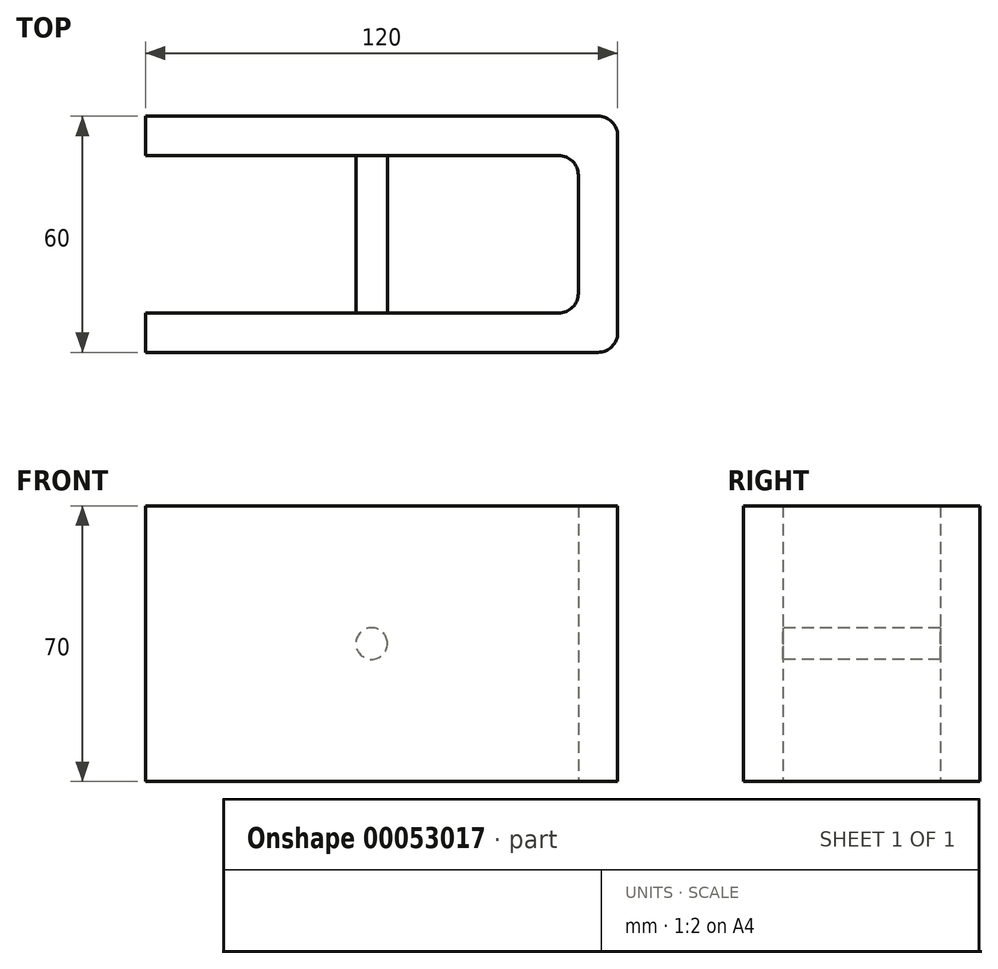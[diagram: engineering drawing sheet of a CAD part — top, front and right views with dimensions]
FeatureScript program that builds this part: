
annotation { "Feature Type Name" : "Feature", "Feature Type Description" : "" }
export const myFeature = defineFeature(function(context is Context, id is Id, definition is map)
    precondition{}
    {
        {
            var Q0;
            Q0=qCreatedBy(makeId("Top.planeOp"),FACE);
            var sketch = newSketch(context, id + "F0", { "sketchPlane" : qUnion([Q0])});
            skLineSegment(sketch, "E0", {"start": v(-61.74, 34.03) * mm, "end": v(53.26, 34.03) * mm});
            skLineSegment(sketch, "E1", {"start": v(43.26, 24.03) * mm, "end": v(-61.74, 24.03) * mm});
            skLineSegment(sketch, "E2", {"start": v(-61.74, 24.03) * mm, "end": v(-61.74, 34.03) * mm});
            skLineSegment(sketch, "E3", {"start": v(-61.74, -15.97) * mm, "end": v(-61.74, -25.97) * mm});
            skLineSegment(sketch, "E4", {"start": v(-61.74, -25.97) * mm, "end": v(53.26, -25.97) * mm});
            skLineSegment(sketch, "E5", {"start": v(43.26, -15.97) * mm, "end": v(-61.74, -15.97) * mm});
            skLineSegment(sketch, "E6", {"start": v(48.26, 19.03) * mm, "end": v(48.26, -10.97) * mm});
            skLineSegment(sketch, "E7", {"start": v(58.26, 29.03) * mm, "end": v(58.26, -20.97) * mm});
            skPoint(sketch, "E8.visualSharp", {"position": v(58.26, 34.03) * mm});
            skArc(sketch, "E8.filletArc", {"start": v(58.26, 29.03) * mm, "mid": v(56.8, 32.56) * mm, "end": v(53.26, 34.03) * mm});
            skPoint(sketch, "E9.visualSharp", {"position": v(48.26, 24.03) * mm});
            skArc(sketch, "E9.filletArc", {"start": v(48.26, 19.03) * mm, "mid": v(46.8, 22.56) * mm, "end": v(43.26, 24.03) * mm});
            skPoint(sketch, "E10.visualSharp", {"position": v(48.26, -15.97) * mm});
            skArc(sketch, "E10.filletArc", {"start": v(43.26, -15.97) * mm, "mid": v(46.8, -14.5) * mm, "end": v(48.26, -10.97) * mm});
            skPoint(sketch, "E11.visualSharp", {"position": v(58.26, -25.97) * mm});
            skArc(sketch, "E11.filletArc", {"start": v(53.26, -25.97) * mm, "mid": v(56.8, -24.5) * mm, "end": v(58.26, -20.97) * mm});
            skSolve(sketch);
        }
        {
            var Q0;
            Q0=makeQuery(id+"F0.imprint","IMPRINT",FACE,{"disambiguationData":[TD([[makeQuery(id+"F0.imprint","IMPRINT",EDGE,{"derivedFrom":sQuery(id+"F0.wireOp",EDGE,"E0")}),-1.0]])]});
            extrude(context, id + "F1", {"entities" : qUnion([Q0]), "depth" : 70 * mm});
        }
        {
            var Q0;
            Q0=makeQuery(id+"F1.opExtrude","SWEPT_FACE",FACE,{"disambiguationData":[OSD([sQuery(id+"F0.wireOp",EDGE,"E4")])]});
            var sketch = newSketch(context, id + "F2", { "sketchPlane" : qUnion([Q0])});
            skLineSegment(sketch, "E12", {"start": v(-61.74, 35) * mm, "end": v(17.47, 35) * mm, "construction": true});
            skLineSegment(sketch, "E13", {"start": v(-4.24, 70) * mm, "end": v(-4.24, 15.7) * mm, "construction": true});
            skCircle(sketch, "E14", {"center": v(-4.24, 35) * mm, "radius": 4 * mm});
            skSolve(sketch);
        }
        {
            var Q0;
            Q0=makeQuery(id+"F2.imprint","IMPRINT",FACE,{"disambiguationData":[TD([[makeQuery(id+"F2.imprint","IMPRINT",EDGE,{"derivedFrom":sQuery(id+"F2.wireOp",EDGE,"E14")}),1.0]])]});
            var Q1;
            Q1=makeQuery(id+"F1.opExtrude","SWEPT_FACE",FACE,{"disambiguationData":[OSD([sQuery(id+"F0.wireOp",EDGE,"E1")])]});
            extrude(context, id + "F3", {"entities" : qUnion([Q0]), "operationType" : NewBodyOperationType.ADD, "endBound" : BoundingType.UP_TO_SURFACE, "oppositeDirection" : true, "endBoundEntityFace" : qUnion([Q1]), "depth" : 25 * mm});
        }
    });
